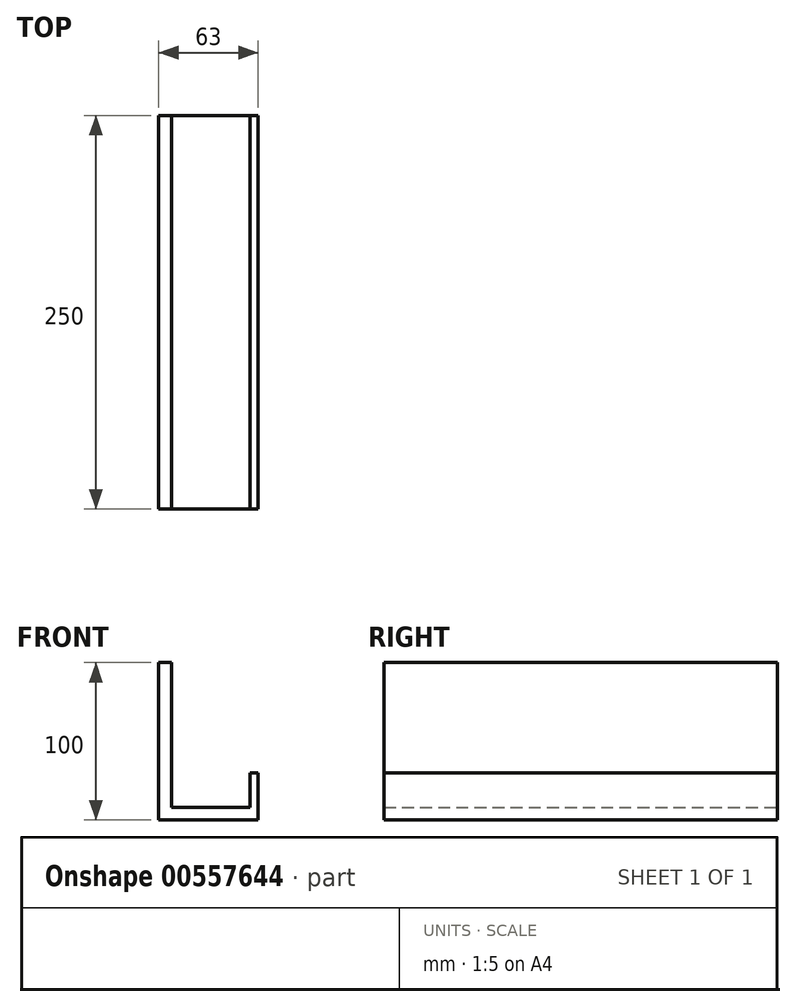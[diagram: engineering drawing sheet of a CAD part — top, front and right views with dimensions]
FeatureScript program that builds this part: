
annotation { "Feature Type Name" : "Feature", "Feature Type Description" : "" }
export const myFeature = defineFeature(function(context is Context, id is Id, definition is map)
    precondition{}
    {
        {
            var Q0;
            Q0=qCreatedBy(makeId("Front.planeOp"),FACE);
            var sketch = newSketch(context, id + "F0", { "sketchPlane" : qUnion([Q0])});
            skLineSegment(sketch, "E0.left", {"start": v(31.5, -20) * mm, "end": v(31.5, -50) * mm});
            skLineSegment(sketch, "E0.right", {"start": v(-31.5, 50) * mm, "end": v(-31.5, -50) * mm});
            skPoint(sketch, "E0.middle", {"position": v(0, 0) * mm});
            skLineSegment(sketch, "E1", {"start": v(-23.5, 50) * mm, "end": v(-31.5, 50) * mm});
            skLineSegment(sketch, "E2", {"start": v(-31.5, -50) * mm, "end": v(31.5, -50) * mm});
            skLineSegment(sketch, "E3", {"start": v(-23.5, 50) * mm, "end": v(-23.5, -42) * mm});
            skLineSegment(sketch, "E4", {"start": v(-23.5, -42) * mm, "end": v(26.5, -42) * mm});
            skLineSegment(sketch, "E5", {"start": v(26.5, -42) * mm, "end": v(26.5, -20) * mm});
            skLineSegment(sketch, "E6", {"start": v(26.5, -20) * mm, "end": v(31.5, -20) * mm});
            skSolve(sketch);
        }
        {
            var Q0;
            Q0 = qSketchRegion(id + "F0", true);
            extrude(context, id + "F1", {"entities" : qUnion([Q0]), "endBound" : BoundingType.SYMMETRIC, "depth" : 250 * mm, "offsetDistance" : 25 * mm});
        }
    });
